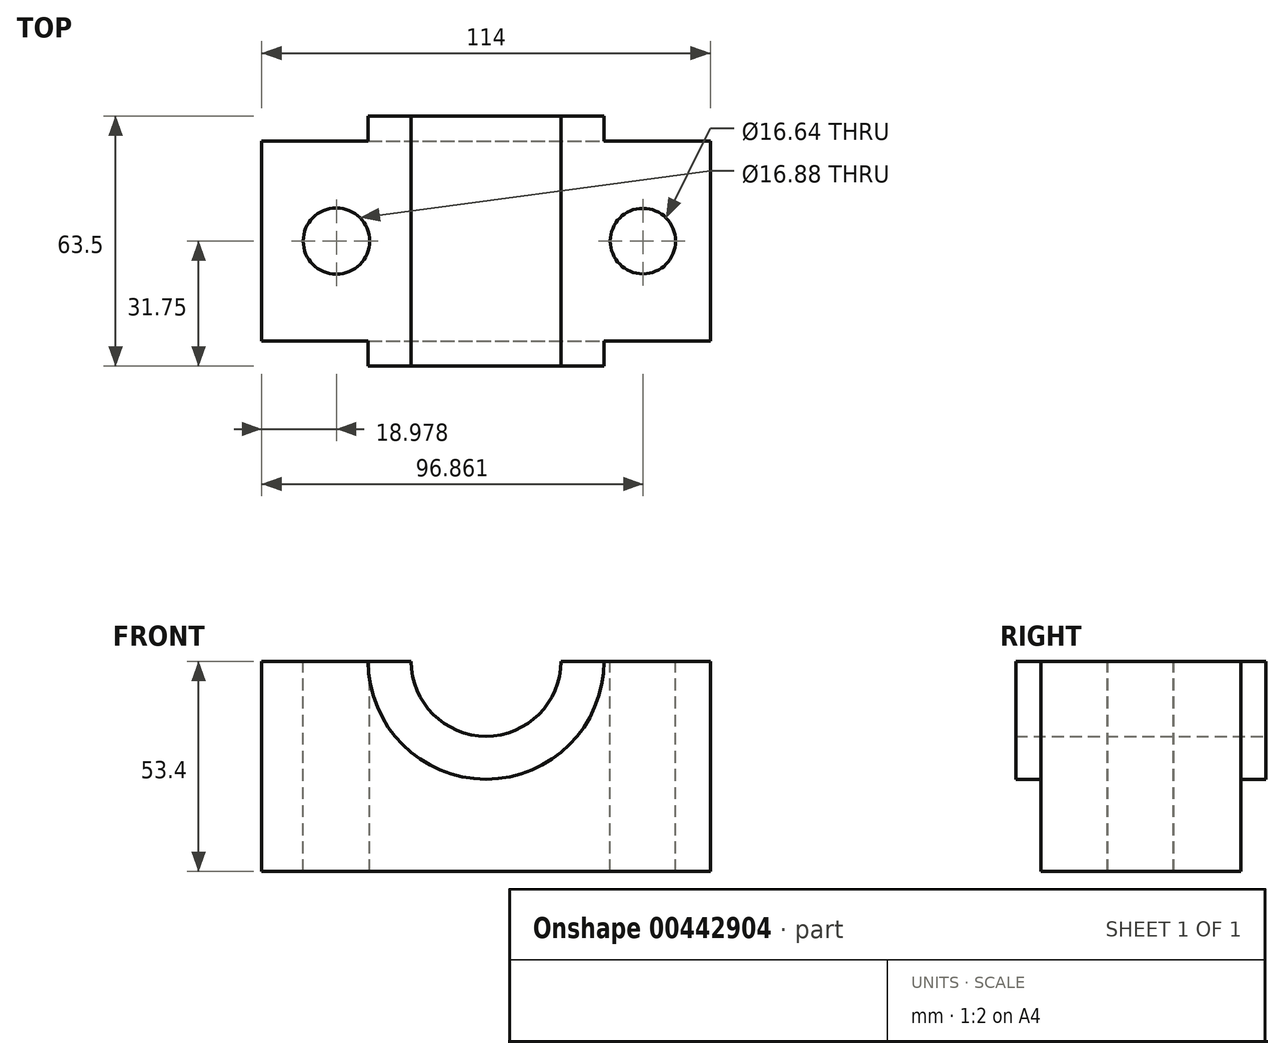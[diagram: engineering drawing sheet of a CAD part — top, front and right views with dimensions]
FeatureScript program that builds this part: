
annotation { "Feature Type Name" : "Feature", "Feature Type Description" : "" }
export const myFeature = defineFeature(function(context is Context, id is Id, definition is map)
    precondition{}
    {
        {
            var Q0;
            Q0=qCreatedBy(makeId("Front.planeOp"),FACE);
            var sketch = newSketch(context, id + "F0", { "sketchPlane" : qUnion([Q0])});
            skLineSegment(sketch, "E0.bottom", {"start": v(-57, 26.7) * mm, "end": v(-29.97, 26.7) * mm});
            skLineSegment(sketch, "E0.top", {"start": v(-57, -26.7) * mm, "end": v(57, -26.7) * mm});
            skLineSegment(sketch, "E0.left", {"start": v(-57, 26.7) * mm, "end": v(-57, -26.7) * mm});
            skLineSegment(sketch, "E0.right", {"start": v(57, 26.7) * mm, "end": v(57, -26.7) * mm});
            skPoint(sketch, "E0.middle", {"position": v(0, 0) * mm});
            skArc(sketch, "E1", {"start": v(-29.97, 26.7) * mm, "mid": v(0, -3.27) * mm, "end": v(29.97, 26.7) * mm});
            skLineSegment(sketch, "E2.trimOffspring", {"start": v(29.97, 26.7) * mm, "end": v(57, 26.7) * mm});
            skArc(sketch, "E3.0", {"start": v(-19.05, 26.7) * mm, "mid": v(0, 7.65) * mm, "end": v(19.05, 26.7) * mm});
            skLineSegment(sketch, "E4", {"start": v(-19.05, 26.7) * mm, "end": v(-29.97, 26.7) * mm});
            skLineSegment(sketch, "E5", {"start": v(19.05, 26.7) * mm, "end": v(29.97, 26.7) * mm});
            skSolve(sketch);
        }
        {
            var Q0;
            Q0=makeQuery(id+"F0.imprint","IMPRINT",FACE,{"disambiguationData":[TD([[makeQuery(id+"F0.imprint","IMPRINT",EDGE,{"derivedFrom":sQuery(id+"F0.wireOp",EDGE,"E0.bottom")}),-1.0]])]});
            extrude(context, id + "F1", {"entities" : qUnion([Q0]), "depth" : 50.8 * mm, "symmetric" : true});
        }
        {
            var Q0;
            Q0=makeQuery(id+"F0.imprint","IMPRINT",FACE,{"disambiguationData":[TD([[makeQuery(id+"F0.imprint","IMPRINT",EDGE,{"derivedFrom":sQuery(id+"F0.wireOp",EDGE,"E1")}),1.0]])]});
            extrude(context, id + "F2", {"entities" : qUnion([Q0]), "operationType" : NewBodyOperationType.ADD, "depth" : 63.5 * mm, "symmetric" : true});
        }
        {
            var Q0;
            Q0=makeQuery(id+"F2.boolean.opBoolean","MERGE",FACE,{"derivedFrom":[makeQuery(id+"F1.opExtrude","SWEPT_FACE",FACE,{"disambiguationData":[OSD([sQuery(id+"F0.wireOp",EDGE,"E0.bottom")])]}),makeQuery(id+"F2.opExtrude","SWEPT_FACE",FACE,{"disambiguationData":[OSD([sQuery(id+"F0.wireOp",EDGE,"E4")])]})]});
            var sketch = newSketch(context, id + "F3", { "sketchPlane" : qUnion([Q0])});
            skCircle(sketch, "E6", {"center": v(-38.02, 0) * mm, "radius": 8.44 * mm});
            skCircle(sketch, "E7", {"center": v(39.86, 0) * mm, "radius": 8.32 * mm});
            skSolve(sketch);
        }
        {
            var Q0;
            Q0=makeQuery(id+"F3.imprint","IMPRINT",FACE,{"disambiguationData":[TD([[makeQuery(id+"F3.imprint","IMPRINT",EDGE,{"derivedFrom":sQuery(id+"F3.wireOp",EDGE,"E6")}),1.0]])]});
            var Q1;
            Q1=makeQuery(id+"F3.imprint","IMPRINT",FACE,{"disambiguationData":[TD([[makeQuery(id+"F3.imprint","IMPRINT",EDGE,{"derivedFrom":sQuery(id+"F3.wireOp",EDGE,"E7")}),1.0]])]});
            extrude(context, id + "F4", {"entities" : qUnion([Q0, Q1]), "operationType" : NewBodyOperationType.REMOVE, "oppositeDirection" : true, "depth" : 74.42 * mm});
        }
    });
